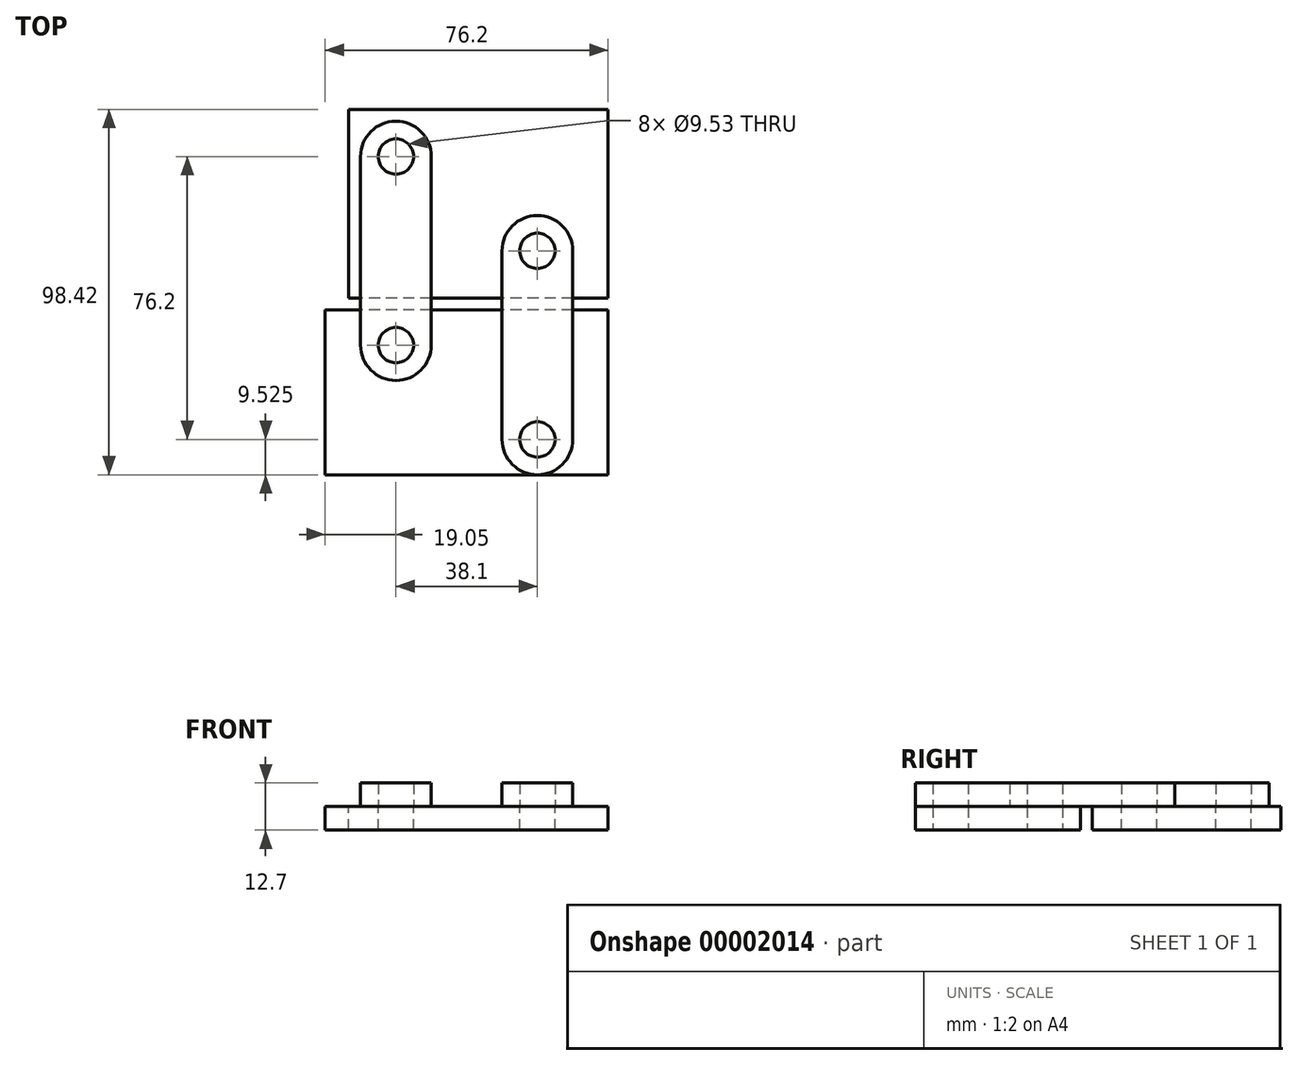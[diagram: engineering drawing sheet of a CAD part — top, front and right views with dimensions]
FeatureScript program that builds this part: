
annotation { "Feature Type Name" : "Feature", "Feature Type Description" : "" }
export const myFeature = defineFeature(function(context is Context, id is Id, definition is map)
    precondition{}
    {
        {
            var Q0;
            Q0=qCreatedBy(makeId("Top.planeOp"),FACE);
            var sketch = newSketch(context, id + "F0", { "sketchPlane" : qUnion([Q0])});
            skLineSegment(sketch, "E0.bottom", {"start": v(0, 0) * mm, "end": v(-95.25, 0) * mm, "construction": true});
            skLineSegment(sketch, "E0.top", {"start": v(0, -44.45) * mm, "end": v(-95.25, -44.45) * mm, "construction": true});
            skLineSegment(sketch, "E0.left", {"start": v(0, 0) * mm, "end": v(0, -44.45) * mm, "construction": true});
            skLineSegment(sketch, "E0.right", {"start": v(-95.25, 0) * mm, "end": v(-95.25, -44.45) * mm, "construction": true});
            skLineSegment(sketch, "E1.bottom", {"start": v(0, 0) * mm, "end": v(-76.2, 0) * mm});
            skLineSegment(sketch, "E1.top", {"start": v(0, 44.45) * mm, "end": v(-76.2, 44.45) * mm});
            skLineSegment(sketch, "E1.left", {"start": v(0, 0) * mm, "end": v(0, 44.45) * mm});
            skLineSegment(sketch, "E1.right", {"start": v(-76.2, 0) * mm, "end": v(-76.2, 44.45) * mm});
            skLineSegment(sketch, "E2", {"start": v(-76.2, 22.23) * mm, "end": v(0, 22.23) * mm, "construction": true});
            skCircle(sketch, "E3", {"center": v(-57.15, 34.92) * mm, "radius": 4.76 * mm});
            skCircle(sketch, "E4", {"center": v(-19.05, 9.53) * mm, "radius": 4.76 * mm});
            skSolve(sketch);
        }
        {
            var Q0;
            Q0=makeQuery(id+"F0.imprint","IMPRINT",FACE,{"disambiguationData":[TD([[makeQuery(id+"F0.imprint","IMPRINT",EDGE,{"derivedFrom":sQuery(id+"F0.wireOp",EDGE,"E1.bottom")}),-1.0]])]});
            extrude(context, id + "F1", {"entities" : qUnion([Q0]), "depth" : 6.35 * mm});
        }
        {
            var Q0;
            Q0=makeQuery(id+"F1.opExtrude","CAP_FACE",FACE,{"disambiguationData":[OSD([sQuery(id+"F0.wireOp",EDGE,"E1.bottom"),sQuery(id+"F0.wireOp",EDGE,"E1.top"),sQuery(id+"F0.wireOp",EDGE,"E1.left"),sQuery(id+"F0.wireOp",EDGE,"E1.right"),sQuery(id+"F0.wireOp",EDGE,"E3"),sQuery(id+"F0.wireOp",EDGE,"E4")])],"isStart":false});
            var sketch = newSketch(context, id + "F2", { "sketchPlane" : qUnion([Q0])});
            skCircle(sketch, "E5.0", {"center": v(-19.05, 9.53) * mm, "radius": 4.76 * mm});
            skCircle(sketch, "E6.0", {"center": v(-57.15, 34.92) * mm, "radius": 4.76 * mm});
            skLineSegment(sketch, "E7", {"start": v(0, 44.45) * mm, "end": v(0, 247.65) * mm, "construction": true});
            skLineSegment(sketch, "E8", {"start": v(-19.05, 9.53) * mm, "end": v(-19.05, 60.32) * mm, "construction": true});
            skLineSegment(sketch, "E9", {"start": v(-57.15, 34.92) * mm, "end": v(-57.15, 85.72) * mm, "construction": true});
            skCircle(sketch, "E10", {"center": v(-19.05, 60.32) * mm, "radius": 4.76 * mm});
            skCircle(sketch, "E11", {"center": v(-57.15, 85.72) * mm, "radius": 4.76 * mm});
            skArc(sketch, "E12", {"start": v(31.75, 9.53) * mm, "mid": v(16.87, 45.45) * mm, "end": v(-19.05, 60.32) * mm, "construction": true});
            skLineSegment(sketch, "E13", {"start": v(-19.05, 9.53) * mm, "end": v(31.75, 9.53) * mm, "construction": true});
            skArc(sketch, "E14", {"start": v(-6.35, 34.92) * mm, "mid": v(-21.23, 70.85) * mm, "end": v(-57.15, 85.72) * mm, "construction": true});
            skLineSegment(sketch, "E15", {"start": v(-57.15, 34.92) * mm, "end": v(-6.35, 34.92) * mm, "construction": true});
            skLineSegment(sketch, "E16", {"start": v(-19.05, 60.32) * mm, "end": v(-57.15, 85.73) * mm, "construction": true});
            skLineSegment(sketch, "E17", {"start": v(31.75, 9.53) * mm, "end": v(-6.35, 34.92) * mm, "construction": true});
            skLineSegment(sketch, "E18.bottom", {"start": v(0, 47.62) * mm, "end": v(-69.85, 47.62) * mm});
            skLineSegment(sketch, "E18.top", {"start": v(0, 98.43) * mm, "end": v(-69.85, 98.43) * mm});
            skLineSegment(sketch, "E18.left", {"start": v(0, 47.62) * mm, "end": v(0, 98.43) * mm});
            skLineSegment(sketch, "E18.right", {"start": v(-69.85, 47.62) * mm, "end": v(-69.85, 98.43) * mm});
            skSolve(sketch);
        }
        {
            var Q0;
            Q0=makeQuery(id+"F2.imprint","IMPRINT",FACE,{"disambiguationData":[TD([[makeQuery(id+"F2.imprint","IMPRINT",EDGE,{"derivedFrom":sQuery(id+"F2.wireOp",EDGE,"E10")}),-1.0]])]});
            extrude(context, id + "F3", {"entities" : qUnion([Q0]), "oppositeDirection" : true, "depth" : 6.35 * mm});
        }
        {
            var Q0;
            Q0=makeQuery(id+"F1.opExtrude","CAP_FACE",FACE,{"disambiguationData":[OSD([sQuery(id+"F0.wireOp",EDGE,"E1.bottom"),sQuery(id+"F0.wireOp",EDGE,"E1.top"),sQuery(id+"F0.wireOp",EDGE,"E1.left"),sQuery(id+"F0.wireOp",EDGE,"E1.right"),sQuery(id+"F0.wireOp",EDGE,"E3"),sQuery(id+"F0.wireOp",EDGE,"E4")])],"isStart":false});
            var sketch = newSketch(context, id + "F4", { "sketchPlane" : qUnion([Q0])});
            skCircle(sketch, "E19.0", {"center": v(-57.15, 34.92) * mm, "radius": 4.76 * mm});
            skArc(sketch, "E20", {"start": v(-47.62, 85.72) * mm, "mid": v(-57.15, 95.25) * mm, "end": v(-66.67, 85.72) * mm});
            skArc(sketch, "E21", {"start": v(-66.67, 34.92) * mm, "mid": v(-57.15, 25.4) * mm, "end": v(-47.62, 34.92) * mm});
            skLineSegment(sketch, "E22", {"start": v(-47.62, 85.72) * mm, "end": v(-47.62, 34.92) * mm});
            skLineSegment(sketch, "E23", {"start": v(-66.67, 34.92) * mm, "end": v(-66.67, 85.72) * mm});
            skCircle(sketch, "E24.0", {"center": v(-57.15, 85.72) * mm, "radius": 4.76 * mm});
            skSolve(sketch);
        }
        {
            var Q0;
            {var subQ5=sQuery(id+"F4.wireOp",EDGE,"E20");Q0=makeQuery(id+"F4.imprint","IMPRINT",FACE,{"disambiguationData":[TD([[makeQuery(id+"F4.imprint","IMPRINT",EDGE,{"derivedFrom":subQ5}),1.0]])]});}
            var Q1;
            Q1=makeQuery(id+"F4.imprint","IMPRINT",FACE,{"disambiguationData":[TD([[makeQuery(id+"F4.imprint","IMPRINT",EDGE,{"derivedFrom":sQuery(id+"F4.wireOp",EDGE,"E19.0")}),-1.0]])]});
            extrude(context, id + "F5", {"entities" : qUnion([Q0, Q1]), "depth" : 6.35 * mm});
        }
        {
            var Q0;
            Q0=makeQuery(id+"F1.opExtrude","CAP_FACE",FACE,{"disambiguationData":[OSD([sQuery(id+"F0.wireOp",EDGE,"E1.bottom"),sQuery(id+"F0.wireOp",EDGE,"E1.top"),sQuery(id+"F0.wireOp",EDGE,"E1.left"),sQuery(id+"F0.wireOp",EDGE,"E1.right"),sQuery(id+"F0.wireOp",EDGE,"E3"),sQuery(id+"F0.wireOp",EDGE,"E4")])],"isStart":false});
            var sketch = newSketch(context, id + "F6", { "sketchPlane" : qUnion([Q0])});
            skCircle(sketch, "E25.0", {"center": v(-19.05, 9.53) * mm, "radius": 4.76 * mm});
            skArc(sketch, "E26", {"start": v(-9.53, 60.32) * mm, "mid": v(-19.05, 69.85) * mm, "end": v(-28.58, 60.32) * mm});
            skArc(sketch, "E27", {"start": v(-28.58, 9.53) * mm, "mid": v(-19.05, 0) * mm, "end": v(-9.53, 9.53) * mm});
            skLineSegment(sketch, "E28", {"start": v(-28.58, 9.53) * mm, "end": v(-28.58, 60.32) * mm});
            skLineSegment(sketch, "E29", {"start": v(-9.53, 60.32) * mm, "end": v(-9.53, 9.53) * mm});
            skCircle(sketch, "E30.0", {"center": v(-19.05, 60.32) * mm, "radius": 4.76 * mm});
            skSolve(sketch);
        }
        {
            var Q0;
            {var subQ5=sQuery(id+"F6.wireOp",EDGE,"E26");Q0=makeQuery(id+"F6.imprint","IMPRINT",FACE,{"disambiguationData":[TD([[makeQuery(id+"F6.imprint","IMPRINT",EDGE,{"derivedFrom":subQ5}),1.0]])]});}
            var Q1;
            Q1=makeQuery(id+"F6.imprint","IMPRINT",FACE,{"disambiguationData":[TD([[makeQuery(id+"F6.imprint","IMPRINT",EDGE,{"derivedFrom":sQuery(id+"F6.wireOp",EDGE,"E25.0")}),-1.0]])]});
            extrude(context, id + "F7", {"entities" : qUnion([Q0, Q1]), "depth" : 6.35 * mm});
        }
    });
